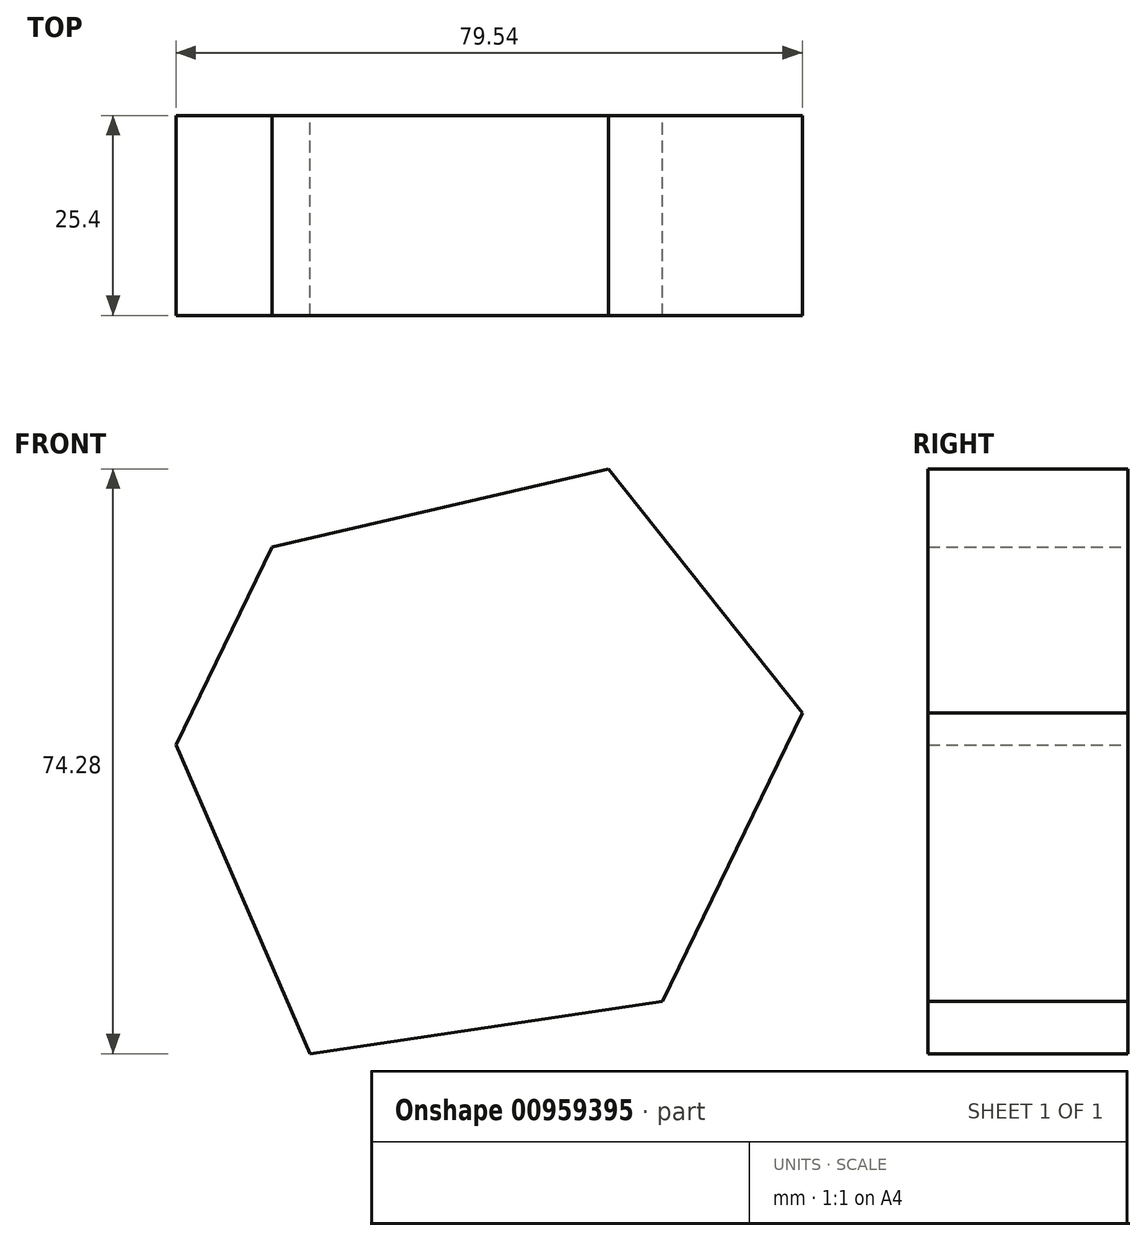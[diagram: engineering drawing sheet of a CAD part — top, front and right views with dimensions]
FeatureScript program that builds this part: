
annotation { "Feature Type Name" : "Feature", "Feature Type Description" : "" }
export const myFeature = defineFeature(function(context is Context, id is Id, definition is map)
    precondition{}
    {
        {
            var Q0;
            Q0=qCreatedBy(makeId("Front.planeOp"),FACE);
            var sketch = newSketch(context, id + "F0", { "sketchPlane" : qUnion([Q0])});
            skLineSegment(sketch, "E0", {"start": v(-42.45, 15.63) * mm, "end": v(-30.24, 40.79) * mm});
            skLineSegment(sketch, "E1", {"start": v(-30.24, 40.79) * mm, "end": v(12.5, 50.69) * mm});
            skLineSegment(sketch, "E2", {"start": v(12.5, 50.69) * mm, "end": v(37.09, 19.7) * mm});
            skLineSegment(sketch, "E3", {"start": v(37.09, 19.7) * mm, "end": v(19.33, -16.93) * mm});
            skLineSegment(sketch, "E4", {"start": v(19.33, -16.93) * mm, "end": v(-25.44, -23.59) * mm});
            skLineSegment(sketch, "E5", {"start": v(-25.44, -23.59) * mm, "end": v(-42.45, 15.63) * mm});
            skSolve(sketch);
        }
        {
            var Q0;
            Q0 = qSketchRegion(id + "F0", true);
            extrude(context, id + "F1", {"entities" : qUnion([Q0]), "depth" : 25.4 * mm, "offsetDistance" : 25.4 * mm});
        }
    });
